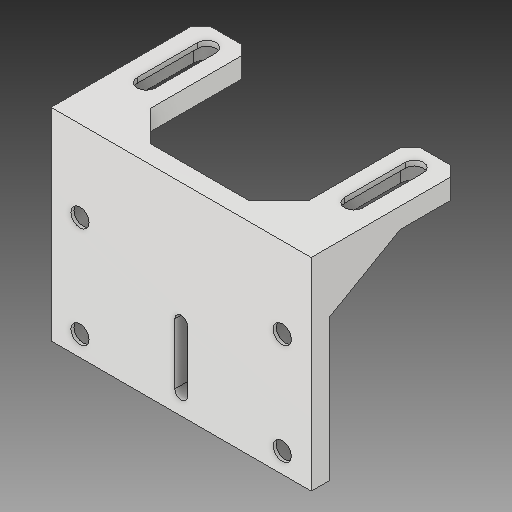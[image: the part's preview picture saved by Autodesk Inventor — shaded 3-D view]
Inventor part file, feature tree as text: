
AUTODESK INVENTOR PART (.ipt)
format: ipt  version: 2019.3 (Build 233278000, 278)  size: 258,560 bytes
history: native  units: mm
features: sketch x7, extrude x5, other x3, rib x2, chamfer x2, reference x1
ambient origin geometry x8: Origin, YZ Plane, XZ Plane, XY Plane, X Axis, Y Axis, Z Axis, Center Point
bodies: Solid1 (feature_tree)
feature tree (20):
  extrude  "Extrusion1"  Depth=9.0mm TaperAngle=0.0deg
  extrude  "Extrusion2"  Depth=10.0mm
  rib  "Rib1"
  rib  "Rib2"
  extrude  "Extrusion3"  Depth=25.0mm
  chamfer  "Chamfer1"  Distance=9.0mm
  chamfer  "Chamfer2"  Distance=4.5mm
  extrude  "Extrusion4"  Depth=7.5mm
  extrude  "Extrusion5"  Depth=7.5mm
  sketch  "Sketch1"  dims[d0=20.0mm d6=9.0mm d7=0.0mm]
  reference  "Reference2"
  sketch  "Sketch2"  dims[d9=65.0mm d10=0.0mm d12=10.0mm]
  sketch  "Sketch3"  dims[d13=25.0mm d14=25.0mm]
  sketch  "Sketch4"  dims[d15=35.0mm]
  sketch  "Sketch5"  dims[d16=20.0mm]
  sketch  "Sketch6"  dims[d17=1.0mm d18=6.0mm d19=0.0mm d20=0.0mm d21=1.0mm d22=1.0mm]
  sketch  "Sketch7"  dims[d23=1.0mm d24=6.0mm d25=0.0mm d26=0.0mm d27=1.0mm d28=1.0mm d30=9.0mm d34=4.5mm d35=7.5mm d36=7.5mm d37=30.0mm d38=10.0mm d39=10.0mm d40=0.0mm d41=3.175mm d42=3.175mm d43=6.35mm d44=3.175mm d45=20.0mm d46=30.0mm d47=15.0mm d48=2.0mm d49=45.0deg d50=5.0mm d51=2.0mm d52=45.0deg d53=9.0mm d54=9.0mm d55=9.0mm d56=9.0mm d57=100.0mm d58=100.0mm d59=50.0mm d60=50.0mm d61=50.0mm d62=50.0mm d63=10.0mm d64=10.0mm d65=14.0mm d66=14.0mm d67=14.0mm d68=14.0mm d69=7.5mm d70=0.0mm d71=13.5mm d73=6.75mm d74=6.75mm d75=6.75mm d76=100.0mm d77=30.0mm d78=30.0mm d79=10.0mm d80=7.5mm d81=0.0mm]
  parser-record x1  (decoder bookkeeping rows leaked as tree rows — omitted from the tree; the rows remain in map.json)
  other  "Assembly.iam"
  other  "Canon_Rebel_T3i:1"
note: 1 file-system path scrubbed to <path> (originals preserved in map.json)
